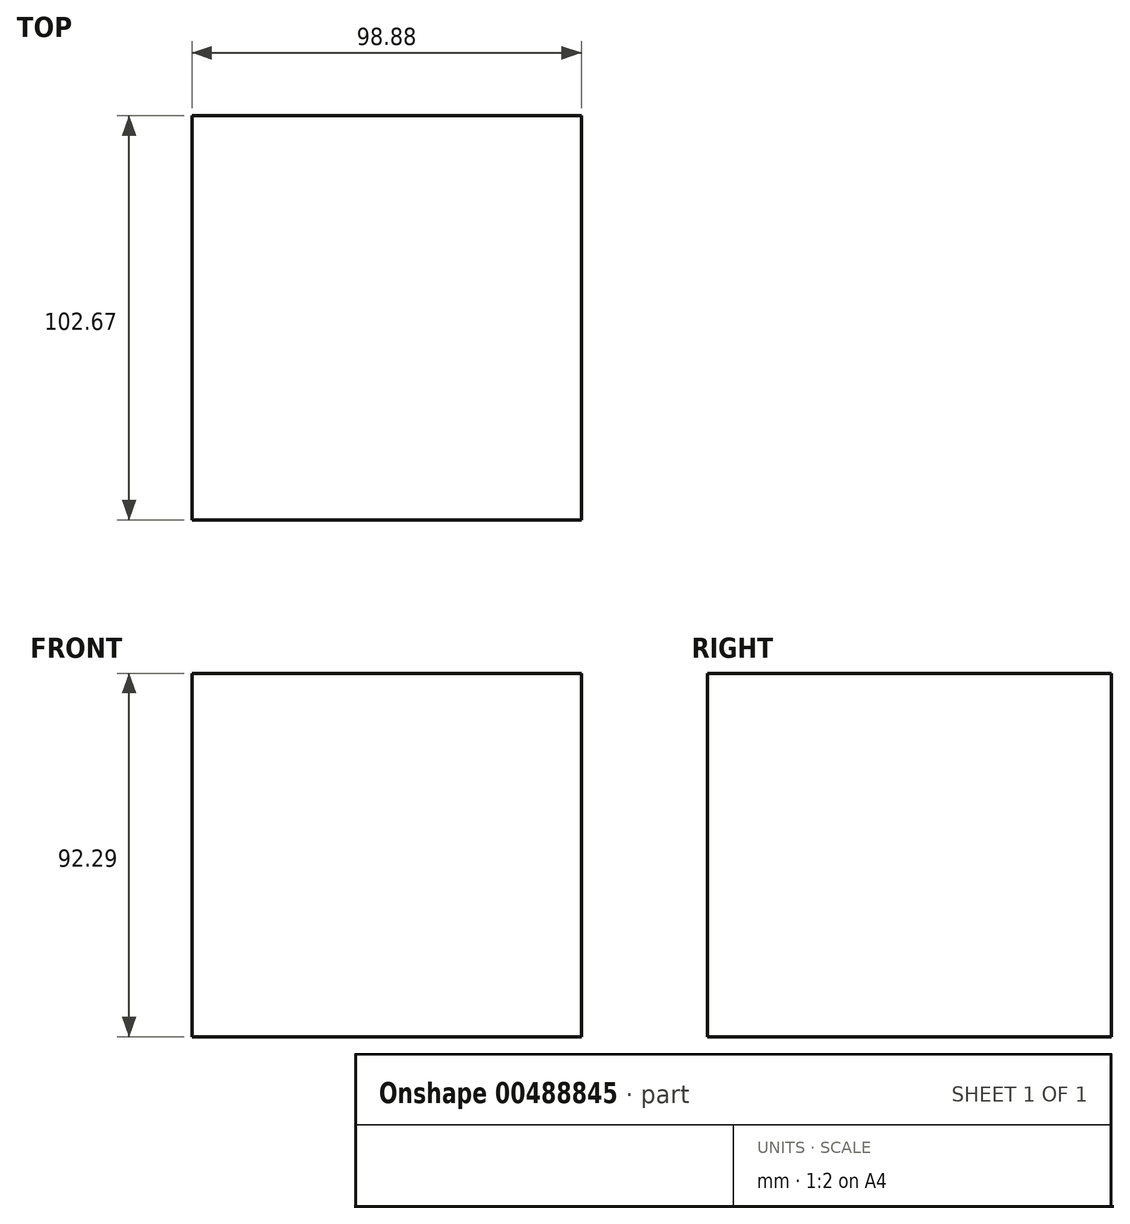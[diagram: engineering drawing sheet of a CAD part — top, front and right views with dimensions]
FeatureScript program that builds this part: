
annotation { "Feature Type Name" : "Feature", "Feature Type Description" : "" }
export const myFeature = defineFeature(function(context is Context, id is Id, definition is map)
    precondition{}
    {
        {
            var Q0;
            Q0=qCreatedBy(makeId("Top.planeOp"),FACE);
            var sketch = newSketch(context, id + "F0", { "sketchPlane" : qUnion([Q0])});
            skLineSegment(sketch, "E0.bottom", {"start": v(-49.26, 53.05) * mm, "end": v(49.62, 53.05) * mm});
            skLineSegment(sketch, "E0.top", {"start": v(-49.26, -49.62) * mm, "end": v(49.62, -49.62) * mm});
            skLineSegment(sketch, "E0.left", {"start": v(-49.26, 53.05) * mm, "end": v(-49.26, -49.62) * mm});
            skLineSegment(sketch, "E0.right", {"start": v(49.62, 53.05) * mm, "end": v(49.62, -49.62) * mm});
            skSolve(sketch);
        }
        {
            var Q0;
            Q0 = qSketchRegion(id + "F0", true);
            extrude(context, id + "F1", {"entities" : qUnion([Q0]), "depth" : 92.3 * mm});
        }
    });
